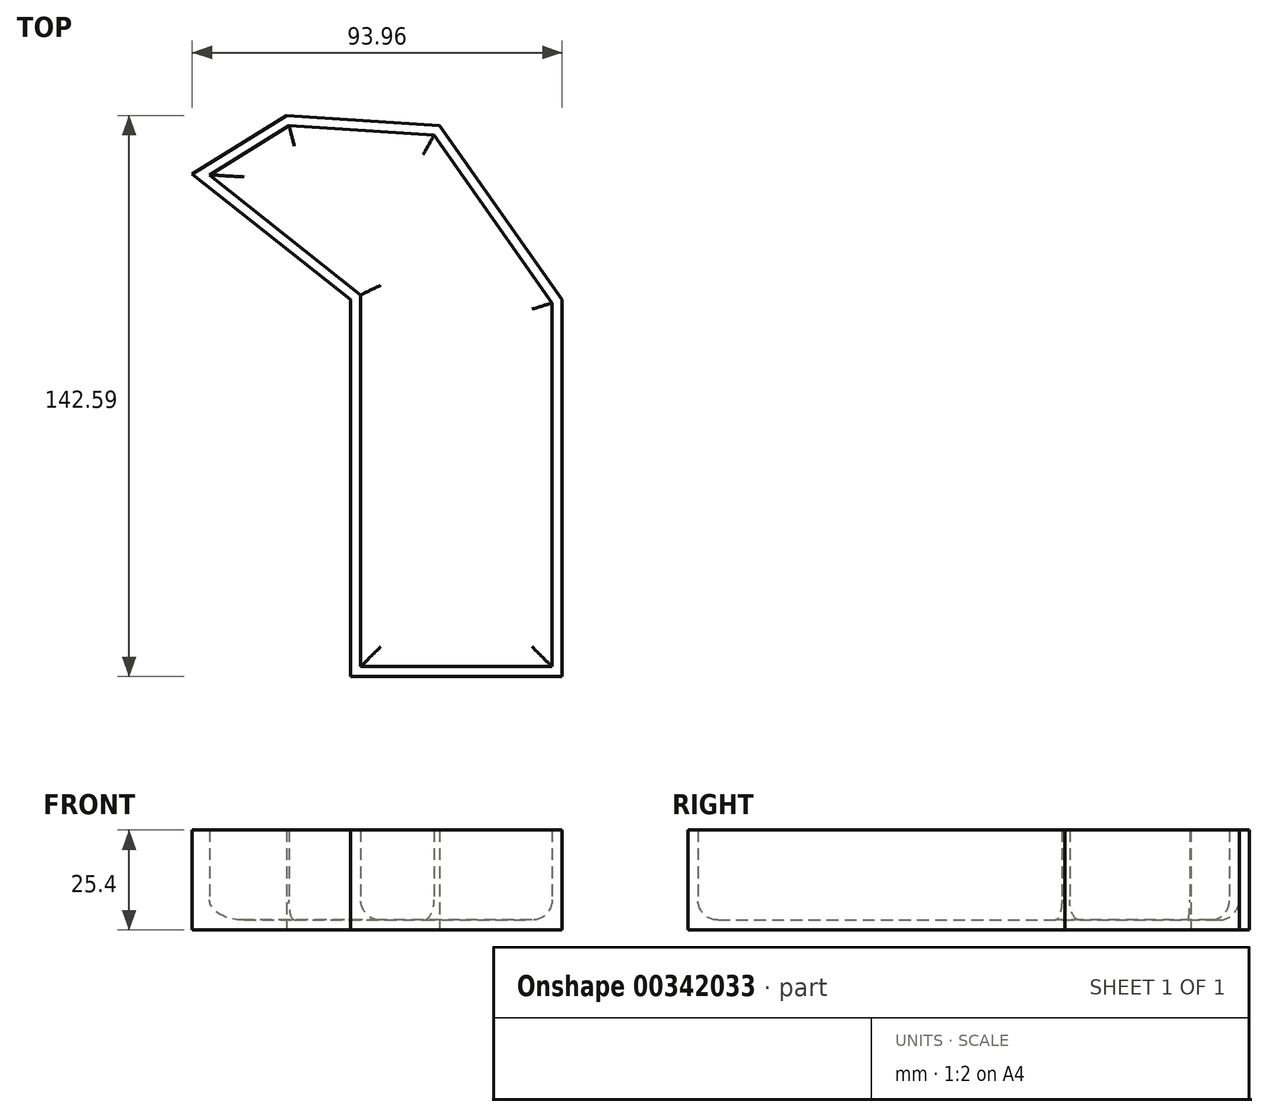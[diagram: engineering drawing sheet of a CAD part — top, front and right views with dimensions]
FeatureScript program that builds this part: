
annotation { "Feature Type Name" : "Feature", "Feature Type Description" : "" }
export const myFeature = defineFeature(function(context is Context, id is Id, definition is map)
    precondition{}
    {
        {
            var Q0;
            Q0=qCreatedBy(makeId("Top.planeOp"),FACE);
            var sketch = newSketch(context, id + "F0", { "sketchPlane" : qUnion([Q0])});
            skLineSegment(sketch, "E0", {"start": v(-50.55, 14) * mm, "end": v(-26.56, 28.84) * mm});
            skLineSegment(sketch, "E1", {"start": v(-26.56, 28.84) * mm, "end": v(12.28, 26.27) * mm});
            skLineSegment(sketch, "E2", {"start": v(12.28, 26.27) * mm, "end": v(43.4, -18) * mm});
            skLineSegment(sketch, "E3", {"start": v(43.4, -18) * mm, "end": v(-10.28, -18) * mm});
            skLineSegment(sketch, "E4", {"start": v(-10.28, -18) * mm, "end": v(-50.55, 14) * mm});
            skSolve(sketch);
        }
        {
            var Q0;
            Q0=makeQuery(id+"F0.imprint","IMPRINT",FACE,{"disambiguationData":[TD([[makeQuery(id+"F0.imprint","IMPRINT",EDGE,{"derivedFrom":sQuery(id+"F0.wireOp",EDGE,"E0")}),-1.0]])]});
            extrude(context, id + "F1", {"entities" : qUnion([Q0]), "depth" : 25.4 * mm});
        }
        {
            var Q0;
            Q0=makeQuery(id+"F1.opExtrude","SWEPT_FACE",FACE,{"disambiguationData":[OSD([sQuery(id+"F0.wireOp",EDGE,"E3")])]});
            extrude(context, id + "F2", {"entities" : qUnion([Q0]), "operationType" : NewBodyOperationType.ADD, "depth" : 95.76 * mm});
        }
        {
            var Q0;
            {var subQ0=sQuery(id+"F0.wireOp",EDGE,"E3");Q0=makeQuery(id+"F2.boolean.opBoolean","MERGE",FACE,{"derivedFrom":[makeQuery(id+"F1.opExtrude","CAP_FACE",FACE,{"disambiguationData":[OSD([sQuery(id+"F0.wireOp",EDGE,"E0"),sQuery(id+"F0.wireOp",EDGE,"E1"),sQuery(id+"F0.wireOp",EDGE,"E2"),subQ0,sQuery(id+"F0.wireOp",EDGE,"E4")])],"isStart":false}),makeQuery(id+"F2.opExtrude","SWEPT_FACE",FACE,{"disambiguationData":[OSD([subQ0]),TDD([makeQuery(id+"F1.opExtrude","CAP_EDGE",EDGE,{"disambiguationData":[OSD([subQ0])],"isStart":false})])]})]});}
            shell(context, id + "F3", {"entities" : qUnion([Q0]), "thickness" : 2.54 * mm});
        }
        {
            var Q0;
            Q0=makeQuery(id+"F3.opShell","OFFSET_FACE",FACE,{"disambiguationData":[OSD([sQuery(id+"F0.wireOp",EDGE,"E0"),sQuery(id+"F0.wireOp",EDGE,"E1"),sQuery(id+"F0.wireOp",EDGE,"E2"),sQuery(id+"F0.wireOp",EDGE,"E3"),sQuery(id+"F0.wireOp",EDGE,"E4")])]});
            fillet(context, id + "F4", {"entities" : qUnion([Q0]), "radius" : 5.08 * mm, "tangentPropagation" : true, "allowEdgeOverflow" : false});
        }
    });
